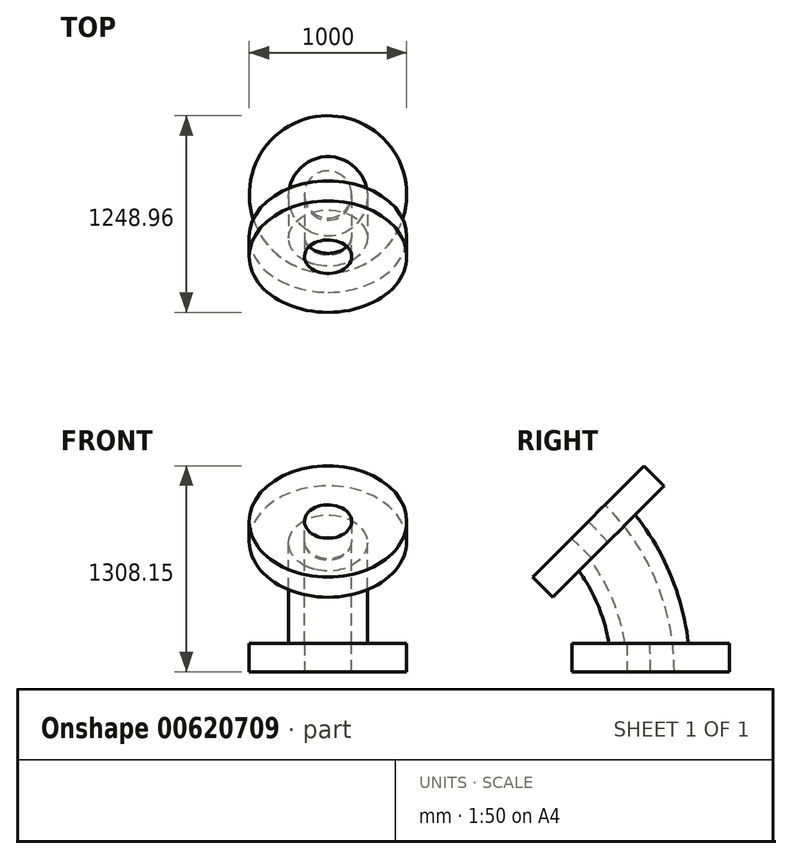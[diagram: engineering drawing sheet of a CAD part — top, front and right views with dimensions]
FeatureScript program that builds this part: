
annotation { "Feature Type Name" : "Feature", "Feature Type Description" : "" }
export const myFeature = defineFeature(function(context is Context, id is Id, definition is map)
    precondition{}
    {
        {
            var Q0;
            Q0=qCreatedBy(makeId("Top.planeOp"),FACE);
            var sketch = newSketch(context, id + "F0", { "sketchPlane" : qUnion([Q0])});
            skCircle(sketch, "E0", {"center": v(0, 0) * mm, "radius": 500 * mm});
            skCircle(sketch, "E1", {"center": v(0, 0) * mm, "radius": 150 * mm});
            skCircle(sketch, "E2", {"center": v(0, 0) * mm, "radius": 250 * mm});
            skSolve(sketch);
        }
        {
            var Q0;
            Q0=qCreatedBy(makeId("Right.planeOp"),FACE);
            var sketch = newSketch(context, id + "F1", { "sketchPlane" : qUnion([Q0])});
            skArc(sketch, "E3", {"start": v(0, 0) * mm, "mid": v(-102.76, 516.62) * mm, "end": v(-395.4, 954.6) * mm});
            skLineSegment(sketch, "E4", {"start": v(-395.4, 954.6) * mm, "end": v(-1350, 0) * mm});
            skLineSegment(sketch, "E5", {"start": v(-1350, 0) * mm, "end": v(0, 0) * mm});
            skSolve(sketch);
        }
        {
            var Q0;
            Q0=makeQuery(id+"F0.imprint","IMPRINT",FACE,{"disambiguationData":[TD([[makeQuery(id+"F0.imprint","IMPRINT",EDGE,{"derivedFrom":sQuery(id+"F0.wireOp",EDGE,"E1")}),-1.0]])]});
            var Q1;
            Q1=sQuery(id+"F1.wireOp",EDGE,"E3");
            sweep(context, id + "F2", {"profiles" : qUnion([Q0]), "path" : qUnion([Q1])});
        }
        {
            var Q0;
            Q0=makeQuery(id+"F0.imprint","IMPRINT",FACE,{"disambiguationData":[TD([[makeQuery(id+"F0.imprint","IMPRINT",EDGE,{"derivedFrom":sQuery(id+"F0.wireOp",EDGE,"E0")}),1.0]])]});
            var Q1;
            Q1=makeQuery(id+"F0.imprint","IMPRINT",FACE,{"disambiguationData":[TD([[makeQuery(id+"F0.imprint","IMPRINT",EDGE,{"derivedFrom":sQuery(id+"F0.wireOp",EDGE,"E1")}),-1.0]])]});
            extrude(context, id + "F3", {"entities" : qUnion([Q0, Q1]), "operationType" : NewBodyOperationType.ADD, "depth" : 180 * mm, "offsetDistance" : 25 * mm});
        }
        {
            var Q0;
            Q0=makeQuery(id+"F2.opSweep","CAP_FACE",FACE,{"disambiguationData":[OSD([sQuery(id+"F0.wireOp",EDGE,"E1"),sQuery(id+"F0.wireOp",EDGE,"E2"),sQuery(id+"F1.wireOp",VERTEX,"E3.end")])],"isStart":false});
            var sketch = newSketch(context, id + "F4", { "sketchPlane" : qUnion([Q0])});
            skCircle(sketch, "E6", {"center": v(0, 395.4) * mm, "radius": 500 * mm});
            skCircle(sketch, "E7", {"center": v(0, 395.4) * mm, "radius": 150 * mm});
            skCircle(sketch, "E8", {"center": v(0, 395.4) * mm, "radius": 250 * mm});
            skSolve(sketch);
        }
        {
            var Q0;
            Q0=makeQuery(id+"F4.imprint","IMPRINT",FACE,{"disambiguationData":[TD([[makeQuery(id+"F4.imprint","IMPRINT",EDGE,{"derivedFrom":sQuery(id+"F4.wireOp",EDGE,"E6")}),1.0]])]});
            var Q1;
            Q1=makeQuery(id+"F4.imprint","IMPRINT",FACE,{"disambiguationData":[TD([[makeQuery(id+"F4.imprint","IMPRINT",EDGE,{"derivedFrom":sQuery(id+"F4.wireOp",EDGE,"E7")}),-1.0]])]});
            extrude(context, id + "F5", {"entities" : qUnion([Q0, Q1]), "operationType" : NewBodyOperationType.ADD, "oppositeDirection" : true, "depth" : 180 * mm, "offsetDistance" : 25 * mm});
        }
    });
